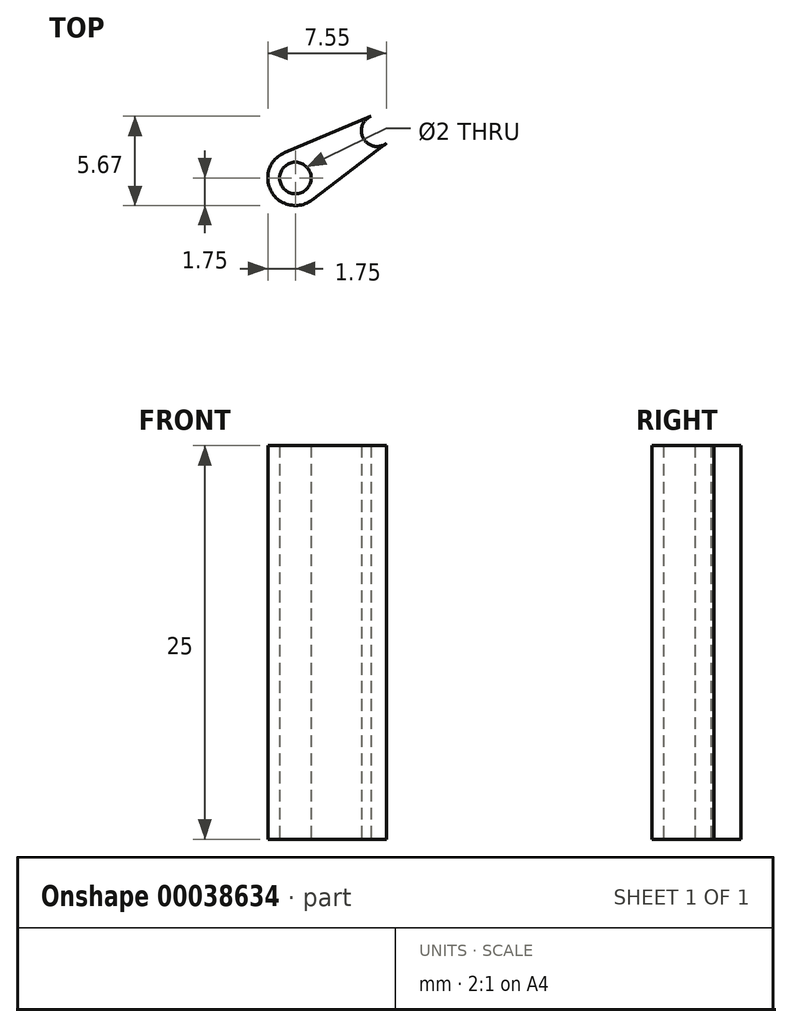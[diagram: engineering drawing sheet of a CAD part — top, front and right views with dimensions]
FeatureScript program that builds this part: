
annotation { "Feature Type Name" : "Feature", "Feature Type Description" : "" }
export const myFeature = defineFeature(function(context is Context, id is Id, definition is map)
    precondition{}
    {
        {
            var Q0;
            Q0=qCreatedBy(makeId("Top.planeOp"),FACE);
            var sketch = newSketch(context, id + "F0", { "sketchPlane" : qUnion([Q0])});
            skCircle(sketch, "E0", {"center": v(0, 0) * mm, "radius": 1 * mm});
            skLineSegment(sketch, "E1", {"start": v(0, 0) * mm, "end": v(5.2, 0) * mm, "construction": true});
            skCircle(sketch, "E2", {"center": v(0, 0) * mm, "radius": 1.75 * mm});
            skLineSegment(sketch, "E3", {"start": v(0, 0) * mm, "end": v(5.2, 3) * mm, "construction": true});
            skCircle(sketch, "E4", {"center": v(5.2, 3) * mm, "radius": 1 * mm});
            skCircle(sketch, "E5", {"center": v(5.2, 3) * mm, "radius": 0.5 * mm});
            skLineSegment(sketch, "E6", {"start": v(4.8, 3.92) * mm, "end": v(-0.68, 1.61) * mm});
            skLineSegment(sketch, "E7", {"start": v(5.8, 2.2) * mm, "end": v(1.06, -1.4) * mm});
            skLineSegment(sketch, "E8.MirrorCS", {"start": v(2.9, 0) * mm, "end": v(1.06, -1.4) * mm});
            skPoint(sketch, "E9.orphan", {"position": v(5.8, 2.2) * mm});
            skCircle(sketch, "E10.2.0.0", {"center": v(66.94, 4.7) * mm, "radius": 2.48 * mm});
            skCircle(sketch, "E10.2.1.0", {"center": v(66.94, 10.7) * mm, "radius": 2.48 * mm});
            skLineSegment(sketch, "E11.bottom", {"start": v(-33.3, 23.46) * mm, "end": v(-31.3, 23.46) * mm});
            skLineSegment(sketch, "E11.top", {"start": v(-33.3, 21.46) * mm, "end": v(-31.3, 21.46) * mm});
            skLineSegment(sketch, "E11.left", {"start": v(-33.3, 23.46) * mm, "end": v(-33.3, 21.46) * mm});
            skLineSegment(sketch, "E11.right", {"start": v(-31.3, 23.46) * mm, "end": v(-31.3, 21.46) * mm});
            skLineSegment(sketch, "E12.bottom", {"start": v(-26.3, 21.46) * mm, "end": v(-24.3, 21.46) * mm});
            skLineSegment(sketch, "E12.top", {"start": v(-26.3, 23.46) * mm, "end": v(-24.3, 23.46) * mm});
            skLineSegment(sketch, "E12.left", {"start": v(-26.3, 21.46) * mm, "end": v(-26.3, 23.46) * mm});
            skLineSegment(sketch, "E12.right", {"start": v(-24.3, 21.46) * mm, "end": v(-24.3, 23.46) * mm});
            skLineSegment(sketch, "E13.bottom", {"start": v(-16.8, 21.46) * mm, "end": v(-14.8, 21.46) * mm});
            skLineSegment(sketch, "E13.top", {"start": v(-16.8, 23.46) * mm, "end": v(-14.8, 23.46) * mm});
            skLineSegment(sketch, "E13.left", {"start": v(-16.8, 21.46) * mm, "end": v(-16.8, 23.46) * mm});
            skLineSegment(sketch, "E13.right", {"start": v(-14.8, 21.46) * mm, "end": v(-14.8, 23.46) * mm});
            skPoint(sketch, "E14", {"position": v(-24.3, 27.69) * mm});
            skLineSegment(sketch, "E15", {"start": v(-54.84, 8.2) * mm, "end": v(-52.5, 12.15) * mm});
            skLineSegment(sketch, "E16", {"start": v(-52.5, 12.15) * mm, "end": v(-57.1, 12.2) * mm});
            skLineSegment(sketch, "E17", {"start": v(-57.1, 12.2) * mm, "end": v(-54.84, 8.2) * mm});
            skLineSegment(sketch, "E18.bottom", {"start": v(-54.73, 21.06) * mm, "end": v(-50.77, 21.06) * mm});
            skLineSegment(sketch, "E18.top", {"start": v(-54.73, 17.1) * mm, "end": v(-50.77, 17.1) * mm});
            skLineSegment(sketch, "E18.left", {"start": v(-54.73, 21.06) * mm, "end": v(-54.73, 17.1) * mm});
            skLineSegment(sketch, "E18.right", {"start": v(-50.77, 21.06) * mm, "end": v(-50.77, 17.1) * mm});
            skLineSegment(sketch, "E19.bottom", {"start": v(-49.73, 31.76) * mm, "end": v(-45.07, 31.76) * mm});
            skLineSegment(sketch, "E19.top", {"start": v(-49.73, 27.1) * mm, "end": v(-45.07, 27.1) * mm});
            skLineSegment(sketch, "E19.left", {"start": v(-49.73, 31.76) * mm, "end": v(-49.73, 27.1) * mm});
            skLineSegment(sketch, "E19.right", {"start": v(-45.07, 31.76) * mm, "end": v(-45.07, 27.1) * mm});
            skSolve(sketch);
        }
        {
            var Q0;
            Q0=makeQuery(id+"F0.imprint","IMPRINT",FACE,{"disambiguationData":[TD([[makeQuery(id+"F0.imprint","IMPRINT",EDGE,{"derivedFrom":sQuery(id+"F0.wireOp",EDGE,"E0")}),-1.0]])]});
            var Q1;
            {var subQ2=sQuery(id+"F0.wireOp",EDGE,"E6");Q1=makeQuery(id+"F0.imprint","IMPRINT",FACE,{"disambiguationData":[TD([[makeQuery(id+"F0.imprint","IMPRINT",EDGE,{"derivedFrom":subQ2}),1.0]])]});}
            extrude(context, id + "F1", {"entities" : qUnion([Q0, Q1]), "depth" : 25 * mm});
        }
    });
